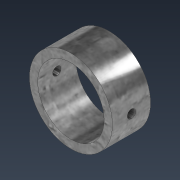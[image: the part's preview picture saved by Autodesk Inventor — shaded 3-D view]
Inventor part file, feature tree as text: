
AUTODESK INVENTOR PART (.ipt)
format: ipt  version: 2022 (Build 260153000, 153)  size: 117,248 bytes
history: native  units: mm
features: extrude x2, sketch x2
ambient origin geometry x8: Origin, YZ Plane, XZ Plane, XY Plane, X Axis, Y Axis, Z Axis, Center Point
bodies: Solid1 (feature_tree)
feature tree (4):
  extrude  "Extrusion1"  Depth=50.0mm
  extrude  "Extrusion2"  Depth=11.5mm
  sketch  "Sketch1"  dims[d0=40.0mm d1=50.0mm]
  sketch  "Sketch2"  dims[d2=23.0mm d3=0.0mm d4=11.5mm d5=5.0mm d6=23.0mm d7=0.0mm]
